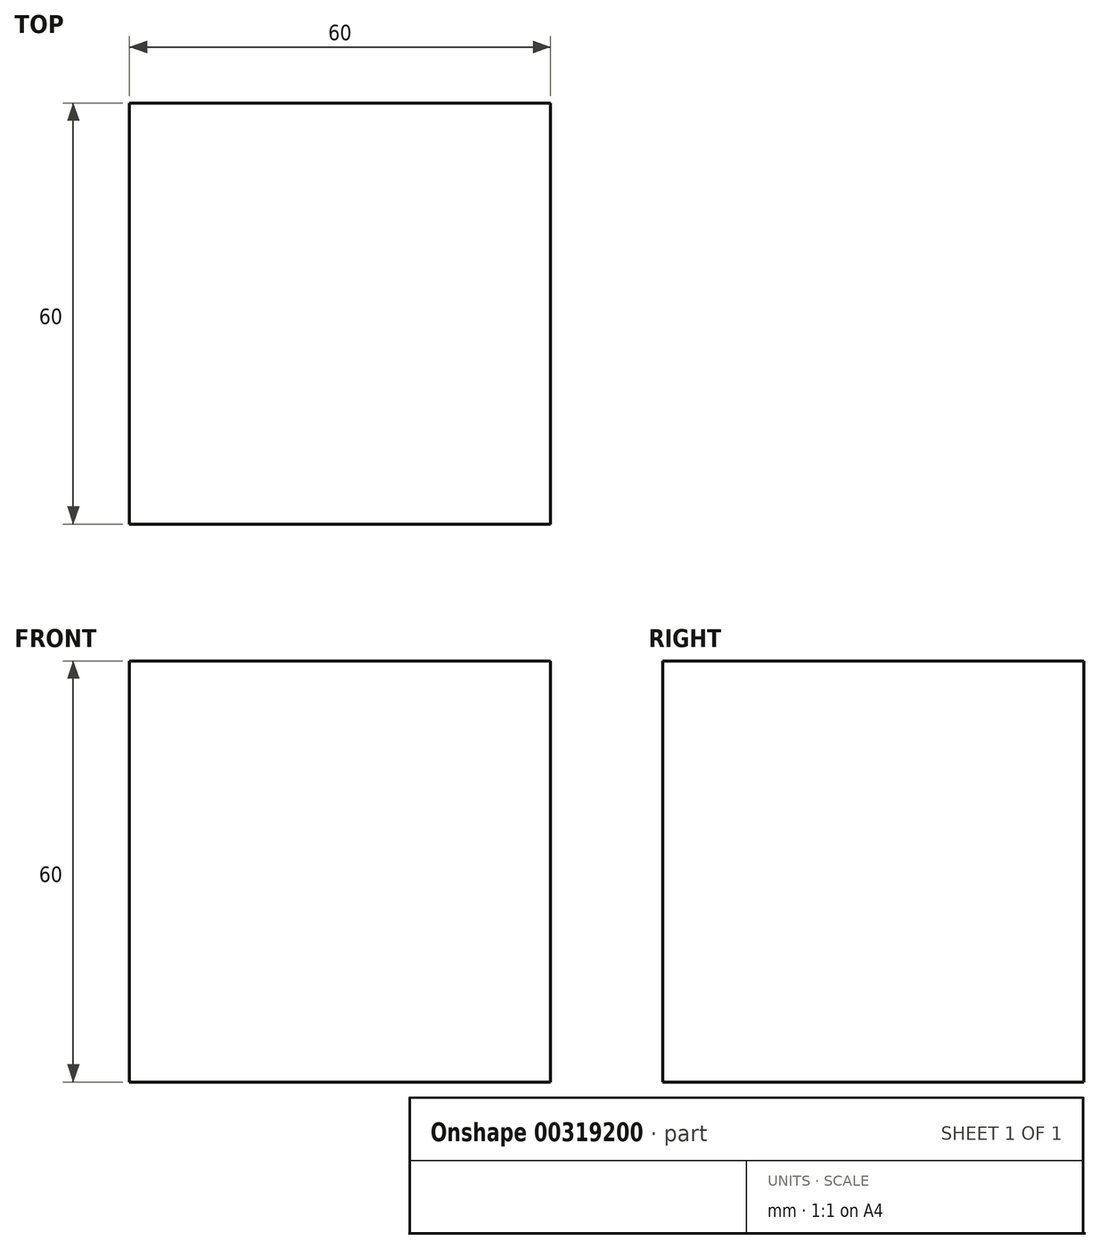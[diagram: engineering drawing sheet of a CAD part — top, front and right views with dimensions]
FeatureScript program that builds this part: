
annotation { "Feature Type Name" : "Feature", "Feature Type Description" : "" }
export const myFeature = defineFeature(function(context is Context, id is Id, definition is map)
    precondition{}
    {
        {
            var Q0;
            Q0=qCreatedBy(makeId("Front.planeOp"),FACE);
            var sketch = newSketch(context, id + "F0", { "sketchPlane" : qUnion([Q0])});
            skLineSegment(sketch, "E0.bottom", {"start": v(-74.28, 60) * mm, "end": v(-14.28, 60) * mm});
            skLineSegment(sketch, "E0.top", {"start": v(-74.28, 0) * mm, "end": v(-14.28, 0) * mm});
            skLineSegment(sketch, "E0.left", {"start": v(-74.28, 60) * mm, "end": v(-74.28, 0) * mm});
            skLineSegment(sketch, "E0.right", {"start": v(-14.28, 60) * mm, "end": v(-14.28, 0) * mm});
            skSolve(sketch);
        }
        {
            var Q0;
            Q0 = qSketchRegion(id + "F0", true);
            extrude(context, id + "F1", {"entities" : qUnion([Q0]), "depth" : 60 * mm});
        }
    });
